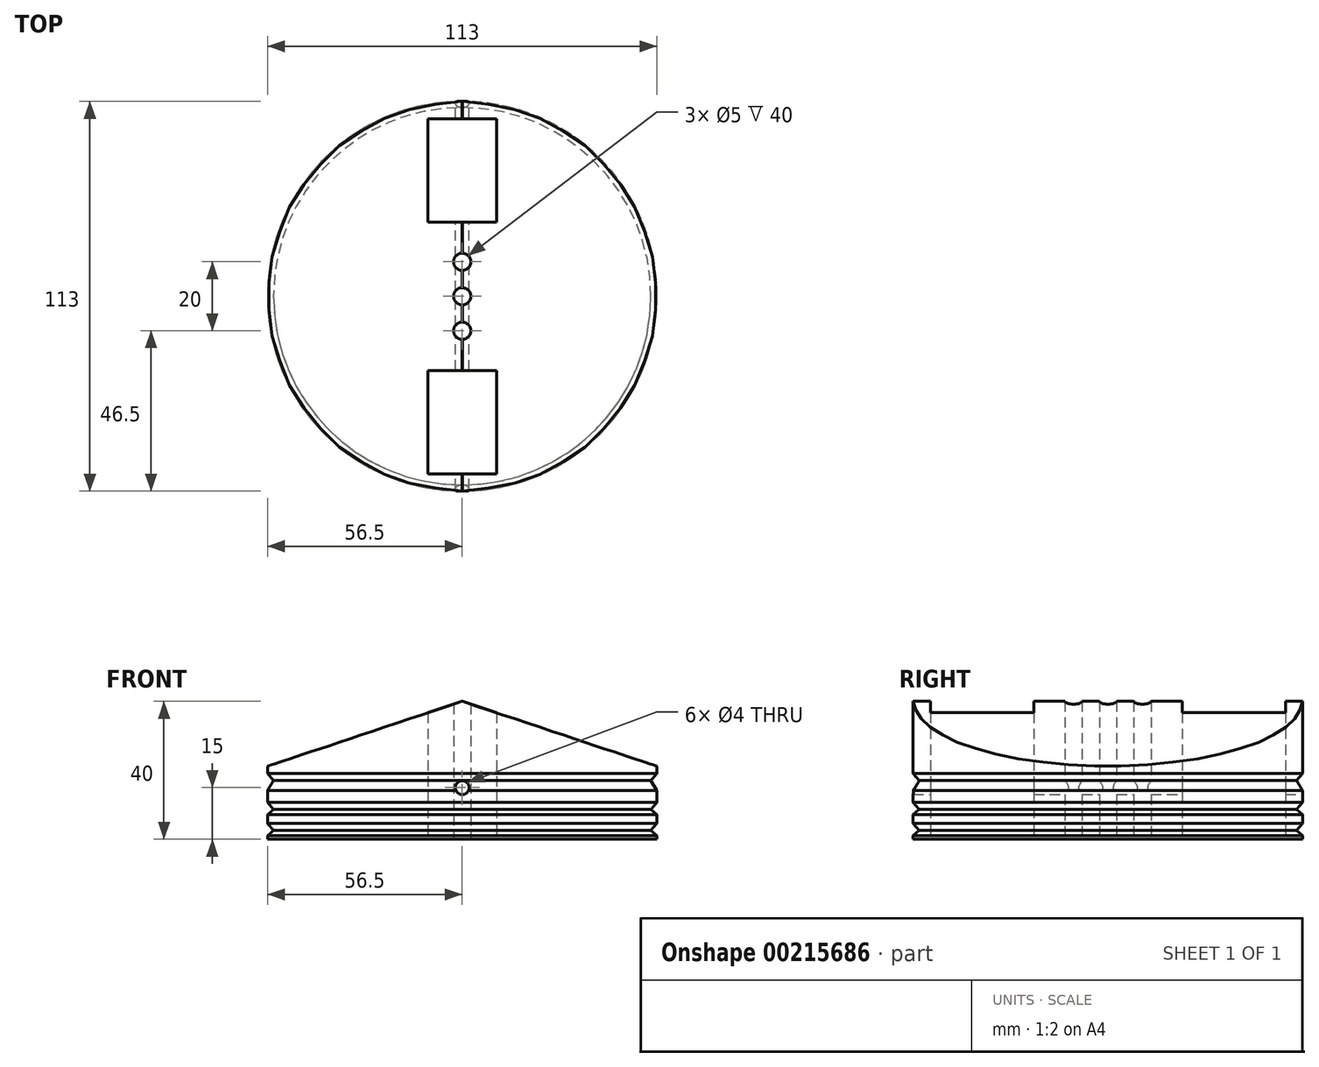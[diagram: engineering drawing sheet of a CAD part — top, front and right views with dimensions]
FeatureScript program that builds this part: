
annotation { "Feature Type Name" : "Feature", "Feature Type Description" : "" }
export const myFeature = defineFeature(function(context is Context, id is Id, definition is map)
    precondition{}
    {
        {
            var Q0;
            Q0=qCreatedBy(makeId("Top.planeOp"),FACE);
            var sketch = newSketch(context, id + "F0", { "sketchPlane" : qUnion([Q0])});
            skCircle(sketch, "E0", {"center": v(0, 0) * mm, "radius": 56.5 * mm});
            skSolve(sketch);
        }
        {
            var Q0;
            Q0 = qSketchRegion(id + "F0", true);
            extrude(context, id + "F1", {"entities" : qUnion([Q0]), "depth" : 40 * mm});
        }
        {
            var Q0;
            Q0=qCreatedBy(makeId("Front.planeOp"),FACE);
            var sketch = newSketch(context, id + "F2", { "sketchPlane" : qUnion([Q0])});
            skLineSegment(sketch, "E1", {"start": v(0, 40.03) * mm, "end": v(-60, 20) * mm});
            skLineSegment(sketch, "E2", {"start": v(-60, 20) * mm, "end": v(-60, 50.03) * mm});
            skLineSegment(sketch, "E3", {"start": v(-60, 50.03) * mm, "end": v(0, 50.03) * mm});
            skLineSegment(sketch, "E4", {"start": v(0, 50.03) * mm, "end": v(60, 50.03) * mm});
            skLineSegment(sketch, "E5", {"start": v(60, 50.03) * mm, "end": v(60, 20) * mm});
            skLineSegment(sketch, "E6", {"start": v(60, 20) * mm, "end": v(0, 40.03) * mm});
            skSolve(sketch);
        }
        {
            var Q0;
            Q0 = qSketchRegion(id + "F2", true);
            extrude(context, id + "F3", {"entities" : qUnion([Q0]), "operationType" : NewBodyOperationType.REMOVE, "endBound" : BoundingType.THROUGH_ALL, "oppositeDirection" : true, "depth" : 25 * mm, "hasSecondDirection" : true, "secondDirectionBound" : SecondDirectionBoundingType.THROUGH_ALL, "secondDirectionOppositeDirection" : false, "secondDirectionDepth" : 25 * mm});
        }
        {
            var Q0;
            Q0=makeQuery(id+"F1.opExtrude","CAP_FACE",FACE,{"disambiguationData":[OSD([sQuery(id+"F0.wireOp",EDGE,"E0")])],"isStart":true});
            var sketch = newSketch(context, id + "F4", { "sketchPlane" : qUnion([Q0])});
            skCircle(sketch, "E7", {"center": v(0, 0) * mm, "radius": 2.5 * mm});
            skCircle(sketch, "E8", {"center": v(0, -10) * mm, "radius": 2.5 * mm});
            skCircle(sketch, "E9.MirrorC", {"center": v(0, 10) * mm, "radius": 2.5 * mm});
            skLineSegment(sketch, "E10.bottom", {"start": v(-10, 51.5) * mm, "end": v(10, 51.5) * mm});
            skLineSegment(sketch, "E10.top", {"start": v(-10, 21.5) * mm, "end": v(10, 21.5) * mm});
            skLineSegment(sketch, "E10.left", {"start": v(-10, 51.5) * mm, "end": v(-10, 21.5) * mm});
            skLineSegment(sketch, "E10.right", {"start": v(10, 51.5) * mm, "end": v(10, 21.5) * mm});
            skLineSegment(sketch, "E11.MirrorCS", {"start": v(-10, -21.5) * mm, "end": v(10, -21.5) * mm});
            skLineSegment(sketch, "E12.MirrorCS", {"start": v(-10, -51.5) * mm, "end": v(10, -51.5) * mm});
            skLineSegment(sketch, "E13.MirrorCS", {"start": v(-10, -51.5) * mm, "end": v(-10, -21.5) * mm});
            skLineSegment(sketch, "E14.MirrorCS", {"start": v(10, -51.5) * mm, "end": v(10, -21.5) * mm});
            skSolve(sketch);
        }
        {
            var Q0;
            Q0 = qSketchRegion(id + "F4", true);
            extrude(context, id + "F5", {"entities" : qUnion([Q0]), "operationType" : NewBodyOperationType.REMOVE, "endBound" : BoundingType.THROUGH_ALL, "oppositeDirection" : true, "depth" : 25 * mm});
        }
        {
            var Q0;
            Q0=makeQuery(id+"F5.boolean.opBoolean","COPY",FACE,{"derivedFrom":makeQuery(id+"F5.opExtrude","SWEPT_FACE",FACE,{"disambiguationData":[OSD([sQuery(id+"F4.wireOp",EDGE,"E11.MirrorCS")])]})});
            var sketch = newSketch(context, id + "F6", { "sketchPlane" : qUnion([Q0])});
            skCircle(sketch, "E15", {"center": v(0, 15) * mm, "radius": 2 * mm});
            skSolve(sketch);
        }
        {
            var Q0;
            Q0 = qSketchRegion(id + "F6", true);
            extrude(context, id + "F7", {"entities" : qUnion([Q0]), "operationType" : NewBodyOperationType.REMOVE, "endBound" : BoundingType.THROUGH_ALL, "oppositeDirection" : true, "depth" : 25 * mm, "hasSecondDirection" : true, "secondDirectionBound" : SecondDirectionBoundingType.THROUGH_ALL, "secondDirectionOppositeDirection" : false, "secondDirectionDepth" : 25 * mm});
        }
        {
            var Q0;
            Q0=qCreatedBy(makeId("Front.planeOp"),FACE);
            var sketch = newSketch(context, id + "F8", { "sketchPlane" : qUnion([Q0])});
            skLineSegment(sketch, "E16", {"start": v(-57.73, 20.57) * mm, "end": v(-54.73, 17.04) * mm});
            skLineSegment(sketch, "E17", {"start": v(-54.73, 17.04) * mm, "end": v(-57.73, 12.16) * mm});
            skLineSegment(sketch, "E18", {"start": v(-57.73, 12.16) * mm, "end": v(-54.73, 8.63) * mm});
            skLineSegment(sketch, "E19", {"start": v(-54.73, 8.63) * mm, "end": v(-57.73, 6.08) * mm});
            skLineSegment(sketch, "E20", {"start": v(-57.73, 6.08) * mm, "end": v(-54.73, 2.55) * mm});
            skLineSegment(sketch, "E21", {"start": v(-54.73, 2.55) * mm, "end": v(-57.73, 0) * mm});
            skLineSegment(sketch, "E22", {"start": v(-57.73, 0) * mm, "end": v(-93.43, 0) * mm});
            skLineSegment(sketch, "E23", {"start": v(-93.43, 0) * mm, "end": v(-93.43, 20.57) * mm});
            skLineSegment(sketch, "E24", {"start": v(-93.43, 20.57) * mm, "end": v(-57.73, 20.57) * mm});
            skLineSegment(sketch, "E25", {"start": v(0, 47.57) * mm, "end": v(0, 0) * mm, "construction": true});
            skSolve(sketch);
        }
        {
            var Q0;
            Q0 = qSketchRegion(id + "F8", true);
            var Q1;
            Q1=sQuery(id+"F8.wireOp",EDGE,"E25");
            revolve(context, id + "F9", {"operationType" : NewBodyOperationType.REMOVE, "entities" : qUnion([Q0]), "axis" : qUnion([Q1]), "revolveType" : RevolveType.FULL, "oppositeDirection" : true});
        }
    });
